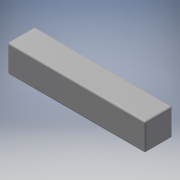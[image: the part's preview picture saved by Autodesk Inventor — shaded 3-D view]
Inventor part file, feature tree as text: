
AUTODESK INVENTOR PART (.ipt)
format: ipt  version: 2017.1 (Build 211199000, 199)  size: 134,144 bytes
history: native  units: mm (DEFAULTED — no unit token found)
features: other x2, sketch x1, fillet x1
ambient origin geometry x8: Origin, YZ Plane, XZ Plane, XY Plane, X Axis, Y Axis, Z Axis, Center Point
bodies: Solid1 (feature_tree), Body1 (feature_tree)
feature tree (4):
  sketch  "Sketch1"  dims[d1=10.0mm d2=-1.5875mm d3=0.4125mm d4=10.0mm d5=0.0mm d9=0.0mm d10=0.0mm d11=0.0mm d12=0.0mm d13=0.127mm]
  other  "IDS_WORKPLANE{1}"
  other  "IDS_WORKPLANE{2}"
  fillet  "Fillet1"  Radius=1.0mm
